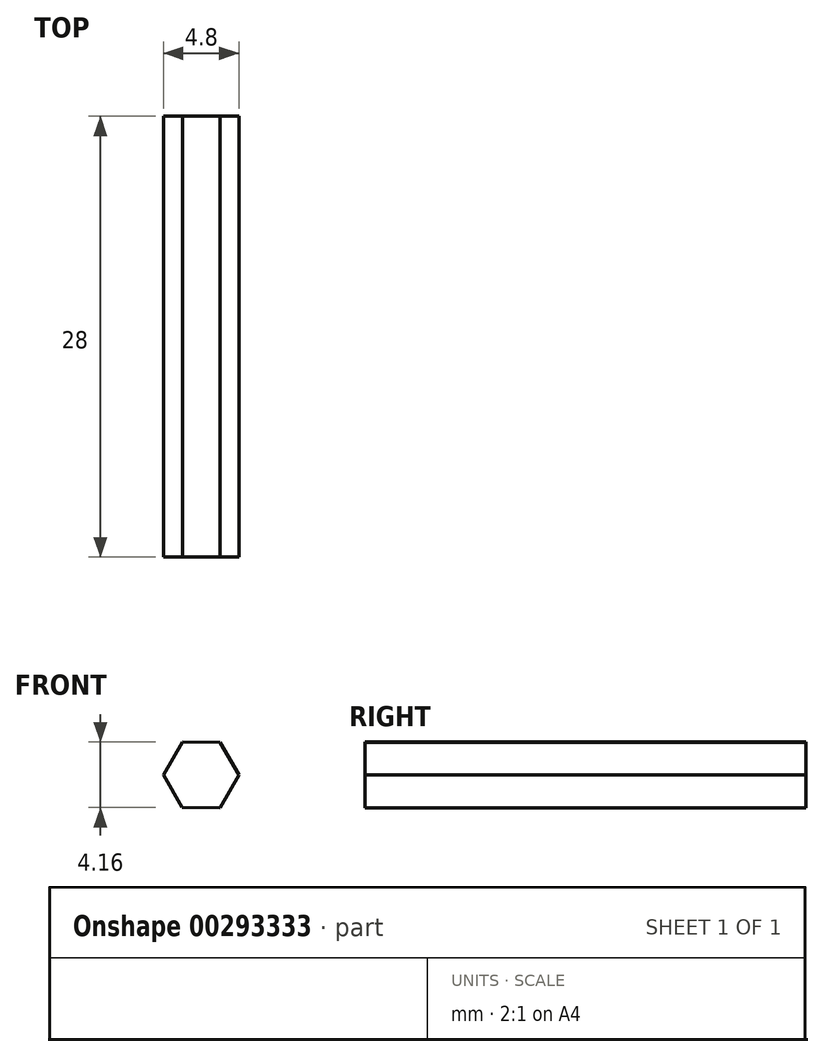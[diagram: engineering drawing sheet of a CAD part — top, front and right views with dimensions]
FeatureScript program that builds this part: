
annotation { "Feature Type Name" : "Feature", "Feature Type Description" : "" }
export const myFeature = defineFeature(function(context is Context, id is Id, definition is map)
    precondition{}
    {
        {
            var Q0;
            Q0=qCreatedBy(makeId("Front.planeOp"),FACE);
            var sketch = newSketch(context, id + "F0", { "sketchPlane" : qUnion([Q0])});
            skCircle(sketch, "E0.cCircle", {"center": v(0, 0) * mm, "radius": 2.08 * mm, "construction": true});
            skLineSegment(sketch, "E0.0", {"start": v(-2.4, 0.01) * mm, "end": v(-1.2, 2.08) * mm});
            skLineSegment(sketch, "E0.1", {"start": v(-1.2, 2.08) * mm, "end": v(1.2, 2.07) * mm});
            skLineSegment(sketch, "E0.2", {"start": v(1.2, 2.07) * mm, "end": v(2.4, -0.01) * mm});
            skLineSegment(sketch, "E0.3", {"start": v(2.4, -0.01) * mm, "end": v(1.2, -2.08) * mm});
            skLineSegment(sketch, "E0.4", {"start": v(1.2, -2.08) * mm, "end": v(-1.2, -2.07) * mm});
            skLineSegment(sketch, "E0.5", {"start": v(-1.2, -2.07) * mm, "end": v(-2.4, 0.01) * mm});
            skPoint(sketch, "E0.0.midPoint", {"position": v(-1.8, 1.05) * mm});
            skSolve(sketch);
        }
        {
            var Q0;
            Q0=makeQuery(id+"F0.imprint","IMPRINT",FACE,{"disambiguationData":[TD([[makeQuery(id+"F0.imprint","IMPRINT",EDGE,{"derivedFrom":sQuery(id+"F0.wireOp",EDGE,"E0.0")}),-1.0]])]});
            extrude(context, id + "F1", {"entities" : qUnion([Q0]), "depth" : 28 * mm});
        }
    });
